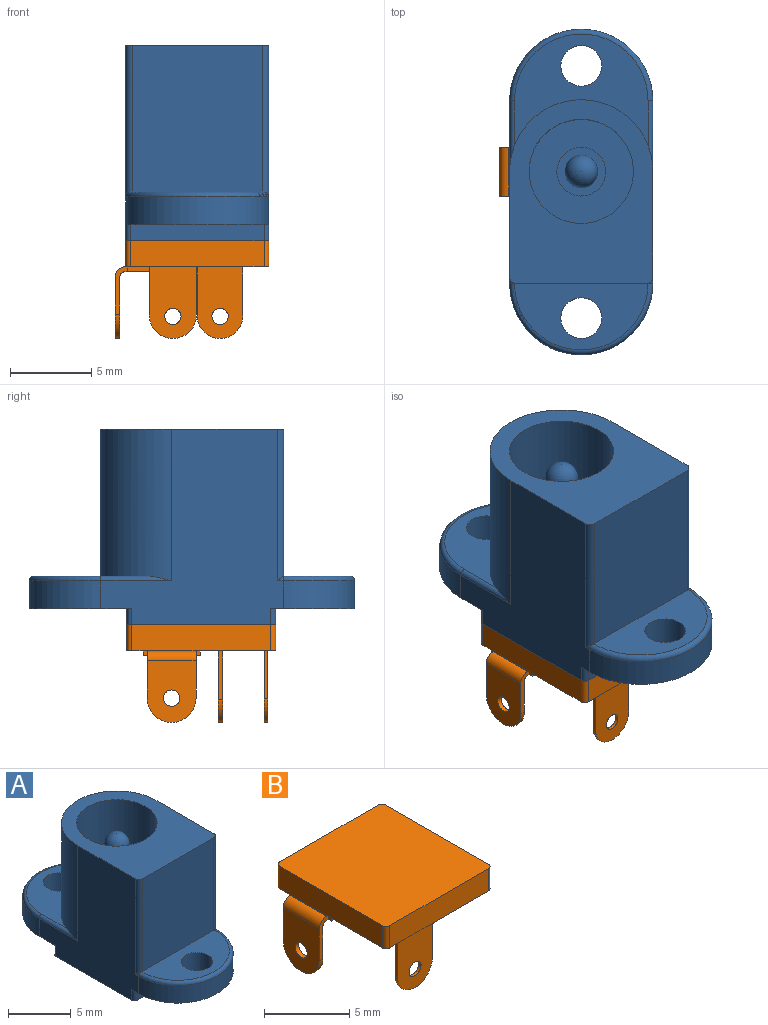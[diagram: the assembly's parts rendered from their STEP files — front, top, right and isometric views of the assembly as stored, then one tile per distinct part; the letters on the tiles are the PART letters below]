
ASSEMBLY  parts=2 mates=1
PART A: 34 faces, bbox 9.5x20.7x12 mm
  f0: cylinder r=3.2mm len=9mm, axis (0,0,-1), area 181mm2, adj f9,f10
  f1: cylinder r=1.25mm len=2.5mm, axis (0,0,1), area 15.7mm2, adj f7,f18
  f2: cylinder r=1.25mm len=2.5mm, axis (0,0,1), area 15.7mm2, adj f6,f17
  f3: cylinder r=1.5mm len=3mm, axis (0,0,-1), area 4.7mm2, adj f8,f9
  f4: cylinder r=1mm len=6.5mm, axis (0,0,-1), area 40.8mm2, adj f5,f8
  f5: sphere r=1mm, area 6.3mm2, adj f4
  f6: plane 8.8x6.3mm, normal (0,0,-1), area 39.6mm2, adj f2,f14,f16,f20,f27,f31,f32
  f7: plane 8.8x5.15mm, normal (0,0,-1), area 29.5mm2, adj f1,f14,f16,f19,f28,f29,f30
  f8: plane 3x3mm, normal (0,0,1), area 3.9mm2, adj f3,f4
  f9: plane 6.4x6.4mm, normal (0,0,1), area 25.1mm2, adj f0,f3
  f10: plane 11.3x8.8mm, normal (0,0,1), area 58.9mm2, adj f0,f11,f12,f13,f14,f15,f16
  f11: cylinder r=0.4mm len=9.3mm, axis (0,0,-1), area 5.7mm2, adj f10,f12,f16,f18,f22,f23
  f12: plane 9x8mm, normal (0,-1,0), area 72mm2, adj f10,f11,f13,f18
  f13: cylinder r=0.4mm len=9.3mm, axis (0,0,-1), area 5.7mm2, adj f10,f12,f14,f18,f21,f22
  f14: plane 12x11.2mm, normal (1,0,0), area 88mm2, adj f6,f7,f10,f13,f15,f19,f20,f21
  f15: cylinder r=4.4mm len=9.3mm, axis (0,0,-1), area 124.9mm2, adj f10,f14,f16,f17,f24,f26
  f16: plane 12x11.2mm, normal (-1,0,0), area 88mm2, adj f6,f7,f10,f11,f15,f19,f20,f23
  f17: plane 8.2x6.85mm, normal (0,0,1), area 27.4mm2, adj f2,f15,f24,f25,f26
  f18: plane 8.2x4.06mm, normal (0,0,1), area 21.1mm2, adj f1,f11,f12,f13,f22
  f19: cylinder r=4.4mm len=8.8mm, axis (0,0,1), area 23.5mm2, adj f7,f14,f16,f22
  f20: cylinder r=4.4mm len=8.8mm, axis (0,0,1), area 23.5mm2, adj f6,f14,f16,f25
  f21: cylinder r=0.3mm len=0.35mm, axis (0,-1,0), area 0.1mm2, adj f13,f14,f22
  f22: torus R=4.1mm, axis (0,0,1), area 6.3mm2, adj f11,f13,f18,f19,f21,f23
  f23: cylinder r=0.3mm len=0.35mm, axis (0,1,0), area 0.1mm2, adj f11,f16,f22
  f24: cylinder r=0.3mm len=4.35mm, axis (0,1,0), area 1.7mm2, adj f15,f16,f17,f25
  f25: torus R=4.1mm, axis (0,0,1), area 6.4mm2, adj f17,f20,f24,f26
  f26: cylinder r=0.3mm len=4.35mm, axis (0,-1,0), area 1.7mm2, adj f14,f15,f17,f25
  f27: cylinder r=0.3mm len=1mm, axis (0,0,1), area 0.5mm2, adj f6,f14,f32,f33
  f28: cylinder r=0.3mm len=1mm, axis (0,0,1), area 0.5mm2, adj f7,f14,f29,f33
  f29: plane 8.2x1mm, normal (0,-1,0), area 8.2mm2, adj f7,f28,f30,f33
  f30: cylinder r=0.3mm len=1mm, axis (0,0,1), area 0.5mm2, adj f7,f16,f29,f33
  f31: cylinder r=0.3mm len=1mm, axis (0,0,1), area 0.5mm2, adj f6,f16,f32,f33
  f32: plane 8.2x1mm, normal (0,1,0), area 8.2mm2, adj f6,f27,f31,f33
  f33: plane 9.15x8.8mm, normal (0,0,-1), area 80.4mm2, adj f14,f16,f27,f28,f29,f30,f31,f32
PART B: 48 faces, bbox 9.5x9.2x6 mm
  f0: cylinder r=0.5mm len=1mm, axis (0,1,0), area 0.6mm2, adj f12,f13
  f1: cylinder r=0.5mm len=1mm, axis (0,1,0), area 0.9mm2, adj f9,f10
  f2: cylinder r=0.5mm len=1mm, axis (-1,0,0), area 0.9mm2, adj f29,f30
  f3: cylinder r=1.75mm len=3.1mm, axis (0,0,1), area 1.3mm2, adj f7,f8,f34,f35
  f4: cylinder r=1mm len=2mm, axis (0,0,1), area 0.9mm2, adj f6,f7
  f5: cylinder r=0.7mm len=1.4mm, axis (0,0,1), area 0.7mm2, adj f6,f42
  f6: torus R=0.85mm, axis (0,0,-1), area 2.5mm2, adj f4,f5
  f7: plane 6.2x3.5mm, normal (0,0,-1), area 15.6mm2, adj f3,f4,f31,f32,f34,f35,f36,f37
  f8: plane 9.15x8.8mm, normal (0,0,-1), area 59.3mm2, adj f3,f9,f10,f11,f12,f13,f14,f15
  f9: plane 4.4x2.8mm, normal (0,-1,0), area 10.7mm2, adj f1,f8,f11,f24,f27
  f10: plane 4.4x2.8mm, normal (0,1,0), area 10.7mm2, adj f1,f8,f11,f24,f27
  f11: plane 3x0.3mm, normal (-1,0,0), area 0.9mm2, adj f8,f9,f10,f27
  f12: plane 4.4x2.9mm, normal (0,-1,0), area 11.1mm2, adj f0,f8,f14,f25,f26
  f13: plane 4.4x2.9mm, normal (0,1,0), area 11.1mm2, adj f0,f8,f14,f25,f26
  f14: plane 2.95x0.2mm, normal (-1,0,0), area 0.6mm2, adj f8,f12,f13,f26
  f15: cylinder r=0.3mm len=1.6mm, axis (0,0,1), area 0.8mm2, adj f8,f16,f22,f23
  f16: plane 8.55x1.6mm, normal (1,0,0), area 13.7mm2, adj f8,f15,f17,f23
  f17: cylinder r=0.3mm len=1.6mm, axis (0,0,1), area 0.8mm2, adj f8,f16,f18,f23
  f18: plane 8.2x1.6mm, normal (0,-1,0), area 13.1mm2, adj f8,f17,f19,f23
  f19: cylinder r=0.3mm len=1.6mm, axis (0,0,1), area 0.8mm2, adj f8,f18,f20,f23
  f20: plane 8.55x1.6mm, normal (-1,0,0), area 13.7mm2, adj f8,f19,f21,f23,f28
  f21: cylinder r=0.3mm len=1.6mm, axis (0,0,1), area 0.8mm2, adj f8,f20,f22,f23
  f22: plane 8.2x1.6mm, normal (0,1,0), area 13.1mm2, adj f8,f15,f21,f23
  f23: plane 9.15x8.8mm, normal (0,0,1), area 80.4mm2, adj f15,f16,f17,f18,f19,f20,f21,f22
  f24: plane 3x0.3mm, normal (1,0,0), area 0.9mm2, adj f8,f9,f10,f27
  f25: plane 2.95x0.2mm, normal (1,0,0), area 0.6mm2, adj f8,f12,f13,f26
  f26: cylinder r=1.45mm len=2.9mm, axis (0,1,0), area 0.9mm2, adj f12,f13,f14,f25
  f27: cylinder r=1.4mm len=2.8mm, axis (0,1,0), area 1.3mm2, adj f9,f10,f11,f24
  f28: plane 3x0.05mm, normal (0,0,1), area 0.1mm2, adj f20,f31,f32,f40
  f29: plane 3.8x3mm, normal (1,0,0), area 9.6mm2, adj f2,f31,f32,f33,f41
  f30: plane 3.8x3mm, normal (-1,0,0), area 9.6mm2, adj f2,f31,f32,f33,f40
  f31: plane 2.9x0.75mm, normal (0,-1,0), area 0.9mm2, adj f7,f8,f28,f29,f30,f33,f38,f40
  f32: plane 2.9x0.75mm, normal (0,1,0), area 0.9mm2, adj f7,f8,f28,f29,f30,f33,f39,f40
  f33: cylinder r=1.5mm len=3mm, axis (-1,0,0), area 1.4mm2, adj f29,f30,f31,f32
  f34: plane 4.3x0.3mm, normal (0,1,0), area 1.3mm2, adj f3,f7,f8,f39
  f35: plane 1.31x0.3mm, normal (0,-1,0), area 0.4mm2, adj f3,f7,f8,f36
  f36: plane 0.4x0.4mm, normal (0.71,-0.71,0), area 0.2mm2, adj f7,f8,f35,f37
  f37: plane 3.7x0.3mm, normal (0,-1,0), area 1.1mm2, adj f7,f8,f36,f38
  f38: plane 0.3x0.25mm, normal (-1,0,0), area 0.1mm2, adj f7,f8,f31,f37
  f39: plane 0.3x0.25mm, normal (-1,0,0), area 0.1mm2, adj f7,f8,f32,f34
  f40: cylinder r=0.6mm len=3mm, axis (0,1,0), area 2.8mm2, adj f28,f30,f31,f32
  f41: cylinder r=0.3mm len=3mm, axis (0,-1,0), area 1.4mm2, adj f7,f29,f31,f32
  f42: plane 1.4x1.4mm, normal (0,0,-1), area 1.5mm2, adj f5
  f43: plane 1.6x0.3mm, normal (-1,0,0), area 0.5mm2, adj f7,f44,f45,f46
  f44: plane 0.7x0.3mm, normal (0,-1,0), area 0.2mm2, adj f7,f43,f46,f47
  f45: plane 0.7x0.3mm, normal (0,1,0), area 0.2mm2, adj f7,f43,f46,f47
  f46: plane 1.6x0.4mm, normal (0,0,-1), area 0.6mm2, adj f43,f44,f45,f47
  f47: plane 1.6x0.3mm, normal (0.71,0,-0.71), area 0.7mm2, adj f7,f44,f45,f46
PLACE A t=(-10.7,-4.38,1.1)mm
PLACE B t=(-10.7,-4.38,1.1)mm
MATE fastened A.f33 <-> B.f23  axis (0,0,-1) through (-10.7,-6.21,-1.9)mm
